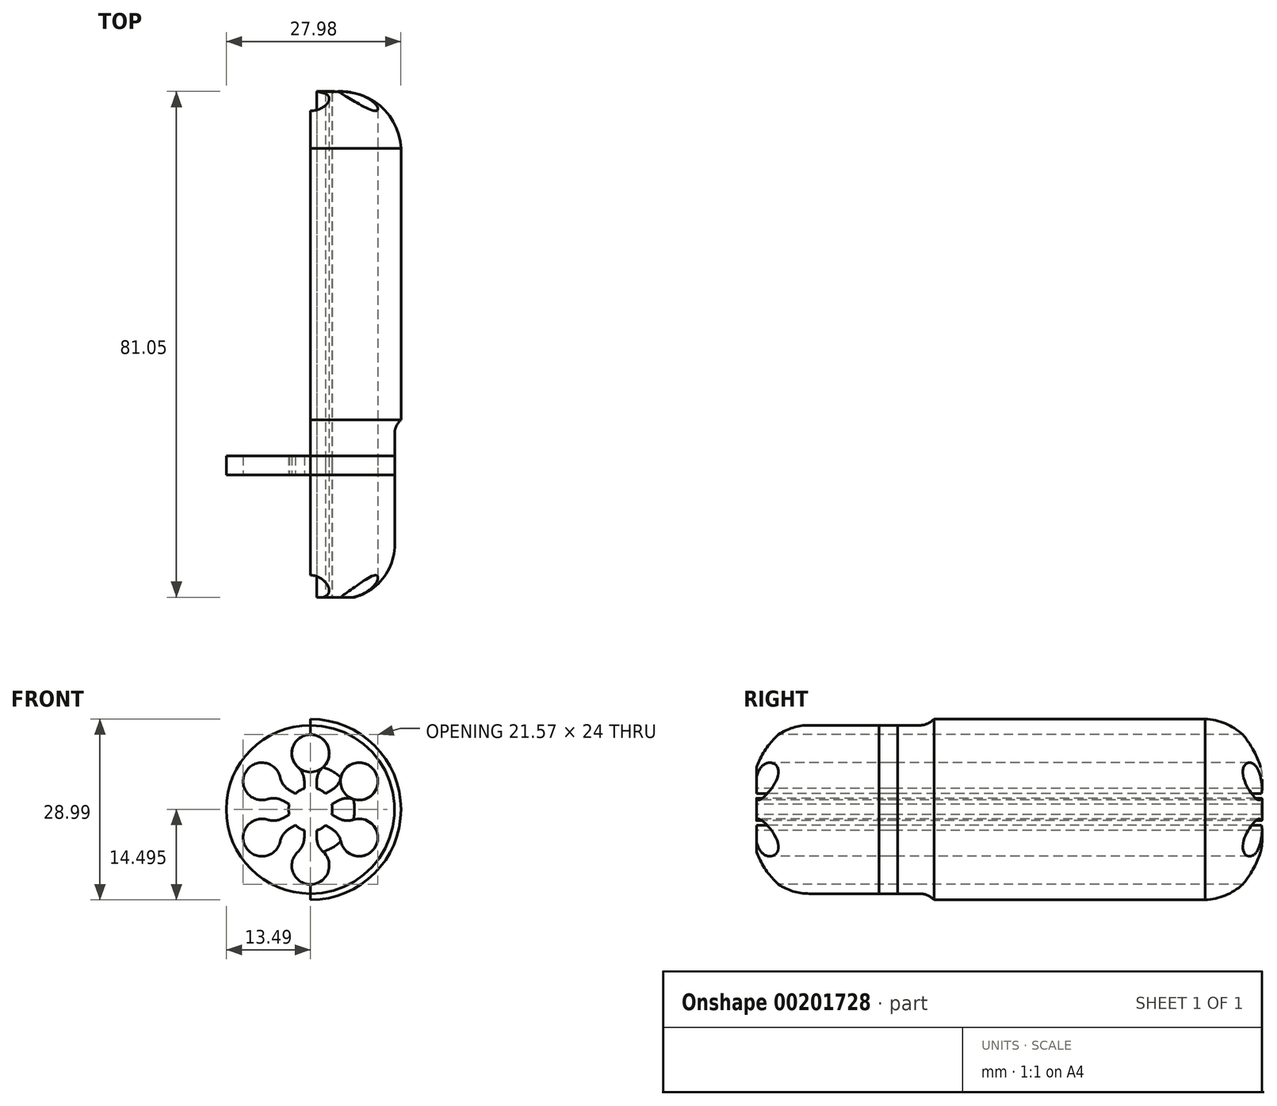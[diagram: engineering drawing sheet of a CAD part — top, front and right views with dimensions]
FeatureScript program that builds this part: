
annotation { "Feature Type Name" : "Feature", "Feature Type Description" : "" }
export const myFeature = defineFeature(function(context is Context, id is Id, definition is map)
    precondition{}
    {
        {
            var Q0;
            Q0=qCreatedBy(makeId("Right.planeOp"),FACE);
            var sketch = newSketch(context, id + "F0", { "sketchPlane" : qUnion([Q0])});
            skLineSegment(sketch, "E0.bottom", {"start": v(-3.13, 33.38) * mm, "end": v(86.87, 33.38) * mm});
            skLineSegment(sketch, "E0.top", {"start": v(-3.13, 32.38) * mm, "end": v(4.08, 32.38) * mm});
            skLineSegment(sketch, "E0.left", {"start": v(-3.13, 33.38) * mm, "end": v(-3.13, 32.38) * mm});
            skLineSegment(sketch, "E0.right", {"start": v(86.87, 33.38) * mm, "end": v(86.87, 32.38) * mm});
            skPoint(sketch, "E0.middle", {"position": v(41.87, 32.88) * mm});
            skLineSegment(sketch, "E1.bottom", {"start": v(86.87, 32.38) * mm, "end": v(81.87, 32.38) * mm, "construction": true});
            skLineSegment(sketch, "E1.top", {"start": v(86.87, 21.38) * mm, "end": v(85.87, 21.38) * mm});
            skLineSegment(sketch, "E1.left", {"start": v(86.87, 32.38) * mm, "end": v(86.87, 21.38) * mm, "construction": true});
            skLineSegment(sketch, "E1.right", {"start": v(81.87, 32.38) * mm, "end": v(81.87, 21.38) * mm, "construction": true});
            skLineSegment(sketch, "E2.bottom", {"start": v(81.87, 32.38) * mm, "end": v(71.87, 32.38) * mm, "construction": true});
            skLineSegment(sketch, "E2.top", {"start": v(81.87, 21.38) * mm, "end": v(71.87, 21.38) * mm, "construction": true});
            skLineSegment(sketch, "E2.right", {"start": v(71.87, 33.38) * mm, "end": v(71.87, 21.38) * mm, "construction": true});
            skLineSegment(sketch, "E3.0", {"start": v(85.87, 22.38) * mm, "end": v(85.37, 22.38) * mm, "construction": true});
            skLineSegment(sketch, "E4.0", {"start": v(85.87, 32.38) * mm, "end": v(85.87, 21.38) * mm, "construction": true});
            skArc(sketch, "E5", {"start": v(82.3, 22.38) * mm, "mid": v(80.84, 28.3) * mm, "end": v(76.33, 32.38) * mm});
            skArc(sketch, "E6", {"start": v(81.87, 21.38) * mm, "mid": v(79.3, 29.1) * mm, "end": v(71.87, 32.38) * mm});
            skLineSegment(sketch, "E7.trimOffspring", {"start": v(76.33, 32.38) * mm, "end": v(86.87, 32.38) * mm});
            skLineSegment(sketch, "E8.top", {"start": v(86.87, 25.38) * mm, "end": v(85.87, 25.38) * mm});
            skLineSegment(sketch, "E8.left", {"start": v(86.87, 23.38) * mm, "end": v(86.87, 25.38) * mm});
            skLineSegment(sketch, "E8.right", {"start": v(85.87, 22.38) * mm, "end": v(85.87, 22.72) * mm, "construction": true});
            skLineSegment(sketch, "E9.bottom", {"start": v(-3.13, 32.38) * mm, "end": v(-2.13, 32.38) * mm, "construction": true});
            skLineSegment(sketch, "E9.top", {"start": v(-3.13, 21.38) * mm, "end": v(-2.13, 21.38) * mm});
            skLineSegment(sketch, "E9.left", {"start": v(-3.13, 32.38) * mm, "end": v(-3.13, 21.38) * mm, "construction": true});
            skLineSegment(sketch, "E9.right", {"start": v(-2.13, 32.38) * mm, "end": v(-2.13, 21.38) * mm, "construction": true});
            skLineSegment(sketch, "E10.bottom", {"start": v(-2.13, 32.38) * mm, "end": v(4.08, 32.38) * mm, "construction": true});
            skLineSegment(sketch, "E10.top", {"start": v(-2.13, 33.38) * mm, "end": v(8.87, 33.38) * mm, "construction": true});
            skLineSegment(sketch, "E10.left", {"start": v(-2.13, 32.38) * mm, "end": v(-2.13, 33.38) * mm, "construction": true});
            skLineSegment(sketch, "E10.right", {"start": v(8.87, 32.38) * mm, "end": v(8.87, 33.38) * mm, "construction": true});
            skArc(sketch, "E11", {"start": v(4.08, 32.38) * mm, "mid": v(-1.17, 27.96) * mm, "end": v(-3.13, 21.38) * mm});
            skArc(sketch, "E12", {"start": v(8.87, 32.38) * mm, "mid": v(1.1, 29.16) * mm, "end": v(-2.13, 21.38) * mm});
            skLineSegment(sketch, "E13.trimOffspring", {"start": v(8.87, 32.38) * mm, "end": v(71.87, 32.38) * mm});
            skLineSegment(sketch, "E14", {"start": v(8.87, 21.38) * mm, "end": v(71.87, 21.38) * mm, "construction": true});
            skLineSegment(sketch, "E15.0", {"start": v(8.87, 17.38) * mm, "end": v(71.87, 17.38) * mm, "construction": true});
            skLineSegment(sketch, "E16.0", {"start": v(86.87, 23.38) * mm, "end": v(85.87, 23.38) * mm, "construction": true});
            skLineSegment(sketch, "E17.0", {"start": v(83.87, 21.38) * mm, "end": v(83.87, 25.38) * mm, "construction": true});
            skLineSegment(sketch, "E18", {"start": v(86.87, 23.38) * mm, "end": v(83.87, 21.38) * mm});
            skLineSegment(sketch, "E19.0", {"start": v(85.87, 23.92) * mm, "end": v(83.57, 22.38) * mm});
            skLineSegment(sketch, "E20.trimOffspring", {"start": v(83.87, 21.38) * mm, "end": v(81.87, 21.38) * mm});
            skLineSegment(sketch, "E21.trimOffspring", {"start": v(83.57, 22.38) * mm, "end": v(82.3, 22.38) * mm});
            skLineSegment(sketch, "E22.trimOffspring", {"start": v(85.87, 23.92) * mm, "end": v(85.87, 25.38) * mm});
            skLineSegment(sketch, "E23.bottom", {"start": v(8.87, 17.38) * mm, "end": v(-3.13, 17.38) * mm, "construction": true});
            skLineSegment(sketch, "E23.top", {"start": v(8.87, 21.38) * mm, "end": v(-3.13, 21.38) * mm, "construction": true});
            skLineSegment(sketch, "E23.left", {"start": v(8.87, 17.38) * mm, "end": v(8.87, 21.38) * mm, "construction": true});
            skLineSegment(sketch, "E23.right", {"start": v(-3.13, 17.38) * mm, "end": v(-3.13, 21.38) * mm, "construction": true});
            skSolve(sketch);
        }
        {
            var Q0;
            Q0=qCreatedBy(makeId("Right.planeOp"),FACE);
            var sketch = newSketch(context, id + "F1", { "sketchPlane" : qUnion([Q0])});
            skLineSegment(sketch, "E24.bottom", {"start": v(-3.13, 33.38) * mm, "end": v(28.58, 33.38) * mm, "construction": true});
            skLineSegment(sketch, "E24.left", {"start": v(-3.13, 33.38) * mm, "end": v(-3.13, 23.38) * mm, "construction": true});
            skLineSegment(sketch, "E24.right", {"start": v(28.58, 33.38) * mm, "end": v(28.58, 33.38) * mm});
            skLineSegment(sketch, "E25", {"start": v(28.58, 32.38) * mm, "end": v(8.84, 32.38) * mm, "construction": true});
            skArc(sketch, "E26", {"start": v(8.84, 32.38) * mm, "mid": v(1.84, 29.83) * mm, "end": v(-1.88, 23.38) * mm, "construction": true});
            skLineSegment(sketch, "E27.0", {"start": v(27.9, 31.88) * mm, "end": v(8.84, 31.88) * mm});
            skArc(sketch, "E28.0", {"start": v(8.84, 31.88) * mm, "mid": v(2.16, 29.45) * mm, "end": v(-1.38, 23.3) * mm});
            skLineSegment(sketch, "E29.0", {"start": v(26.58, 31.38) * mm, "end": v(8.84, 31.38) * mm});
            skArc(sketch, "E30.0", {"start": v(8.84, 30.88) * mm, "mid": v(2.9, 28.77) * mm, "end": v(-0.35, 23.38) * mm, "construction": true});
            skPoint(sketch, "E31.newPointB", {"position": v(28.58, 23.38) * mm});
            skArc(sketch, "E31.filletArc", {"start": v(26.58, 31.38) * mm, "mid": v(27.3, 31.5) * mm, "end": v(27.9, 31.88) * mm});
            skArc(sketch, "E32", {"start": v(8.84, 31.38) * mm, "mid": v(2.64, 29.01) * mm, "end": v(-0.4, 23.12) * mm});
            skLineSegment(sketch, "E33.trimOffspring", {"start": v(-1.37, 23.38) * mm, "end": v(-0.35, 23.38) * mm});
            skSolve(sketch);
        }
        {
            var Q0;
            Q0=qCreatedBy(makeId("Right.planeOp"),FACE);
            var sketch = newSketch(context, id + "F2", { "sketchPlane" : qUnion([Q0])});
            skLineSegment(sketch, "E34", {"start": v(86.87, 23.38) * mm, "end": v(83.87, 21.38) * mm, "construction": true});
            skLineSegment(sketch, "E35", {"start": v(83.87, 21.38) * mm, "end": v(81.87, 21.38) * mm, "construction": true});
            skLineSegment(sketch, "E36.0", {"start": v(86.87, 22.78) * mm, "end": v(84.02, 20.88) * mm});
            skLineSegment(sketch, "E37.0", {"start": v(84.02, 20.88) * mm, "end": v(81.87, 20.88) * mm});
            skLineSegment(sketch, "E38", {"start": v(86.87, 22.78) * mm, "end": v(86.87, 17.38) * mm});
            skLineSegment(sketch, "E39.0", {"start": v(66.87, 20.38) * mm, "end": v(66.87, 17.38) * mm});
            skLineSegment(sketch, "E40.0", {"start": v(81.87, 20.38) * mm, "end": v(66.87, 20.38) * mm});
            skLineSegment(sketch, "E41", {"start": v(71.87, 17.38) * mm, "end": v(66.87, 17.38) * mm});
            skLineSegment(sketch, "E42", {"start": v(71.87, 17.38) * mm, "end": v(86.87, 17.38) * mm});
            skLineSegment(sketch, "E43.0", {"start": v(81.87, 20.88) * mm, "end": v(81.87, 20.38) * mm});
            skSolve(sketch);
        }
        {
            var Q0;
            Q0=qCreatedBy(makeId("Right.planeOp"),FACE);
            var sketch = newSketch(context, id + "F3", { "sketchPlane" : qUnion([Q0])});
            skArc(sketch, "E44", {"start": v(81.87, 21.38) * mm, "mid": v(79.3, 29.1) * mm, "end": v(71.87, 32.38) * mm, "construction": true});
            skArc(sketch, "E45.0", {"start": v(81.3, 20.88) * mm, "mid": v(79.25, 28.4) * mm, "end": v(72.28, 31.88) * mm});
            skLineSegment(sketch, "E46", {"start": v(81.87, 20.38) * mm, "end": v(69.18, 20.38) * mm, "construction": true});
            skLineSegment(sketch, "E47", {"start": v(28.58, 32.38) * mm, "end": v(37.05, 32.38) * mm});
            skLineSegment(sketch, "E48", {"start": v(26.58, 31.38) * mm, "end": v(22.5, 31.38) * mm});
            skArc(sketch, "E49", {"start": v(26.58, 31.38) * mm, "mid": v(27.7, 31.64) * mm, "end": v(28.58, 32.38) * mm});
            skLineSegment(sketch, "E50.0", {"start": v(28.58, 31.88) * mm, "end": v(72.28, 31.88) * mm});
            skArc(sketch, "E51.0", {"start": v(26.58, 30.88) * mm, "mid": v(27.93, 31.2) * mm, "end": v(28.98, 32.08) * mm});
            skLineSegment(sketch, "E52.0", {"start": v(26.58, 30.88) * mm, "end": v(8.74, 30.88) * mm});
            skLineSegment(sketch, "E53.0", {"start": v(81.3, 20.88) * mm, "end": v(0.37, 20.88) * mm});
            skArc(sketch, "E54", {"start": v(8.84, 31.38) * mm, "mid": v(2.74, 29.11) * mm, "end": v(-0.35, 23.38) * mm, "construction": true});
            skArc(sketch, "E55.0", {"start": v(8.83, 30.88) * mm, "mid": v(3.5, 29.1) * mm, "end": v(0.37, 24.44) * mm});
            skLineSegment(sketch, "E56", {"start": v(-2.13, 27.58) * mm, "end": v(-2.13, 15.19) * mm, "construction": true});
            skLineSegment(sketch, "E57.trimOffspring", {"start": v(0.37, 24.44) * mm, "end": v(0.37, 20.88) * mm});
            skSolve(sketch);
        }
        {
            var Q0;
            Q0=qSketchRegion(id+"F3",true);
            var Q1;
            Q1=sQuery(id+"F0.wireOp",EDGE,"E15.0");
            revolve(context, id + "F4", {"entities" : qUnion([Q0]), "axis" : qUnion([Q1]), "revolveType" : RevolveType.ONE_DIRECTION, "angle" : 180 * degree});
        }
        {
            var Q0;
            Q0=qCreatedBy(makeId("Front.planeOp"),FACE);
            var sketch = newSketch(context, id + "F5", { "sketchPlane" : qUnion([Q0])});
            skCircle(sketch, "E58", {"center": v(0, 17.38) * mm, "radius": 14.5 * mm, "construction": true});
            skCircle(sketch, "E59", {"center": v(0, 17.38) * mm, "radius": 3.5 * mm});
            skLineSegment(sketch, "E60", {"start": v(0, 17.38) * mm, "end": v(0, 5.38) * mm, "construction": true});
            skPoint(sketch, "E61", {"position": v(0, 5.38) * mm});
            skPoint(sketch, "E62", {"position": v(-16.26, 26.77) * mm});
            skLineSegment(sketch, "E63.0", {"start": v(-1, 14.03) * mm, "end": v(-1, 12.86) * mm});
            skLineSegment(sketch, "E64.0", {"start": v(1, 14.03) * mm, "end": v(1, 12.86) * mm});
            skArc(sketch, "E65", {"start": v(-2, 10.62) * mm, "mid": v(0, 5.38) * mm, "end": v(2, 10.62) * mm});
            skPoint(sketch, "E66.visualSharp", {"position": v(-1, 11.21) * mm});
            skArc(sketch, "E66.filletArc", {"start": v(-2, 10.62) * mm, "mid": v(-1.26, 11.63) * mm, "end": v(-1, 12.86) * mm});
            skPoint(sketch, "E67.visualSharp", {"position": v(1, 11.21) * mm});
            skArc(sketch, "E67.filletArc", {"start": v(1, 12.86) * mm, "mid": v(1.26, 11.63) * mm, "end": v(2, 10.62) * mm});
            skSolve(sketch);
        }
        {
            var Q0;
            {var subQ0=sQuery(id+"F5.wireOp",EDGE,"E63.0");Q0=makeQuery(id+"F5.imprint","IMPRINT",FACE,{"disambiguationData":[TD([[makeQuery(id+"F5.imprint","IMPRINT",EDGE,{"derivedFrom":subQ0}),1.0]])]});}
            extrude(context, id + "F6", {"entities" : qUnion([Q0]), "oppositeDirection" : true, "depth" : 90 * mm});
        }
        {
            var Q0;
            Q0=qCreatedBy(makeId("Right.planeOp"),FACE);
            var sketch = newSketch(context, id + "F7", { "sketchPlane" : qUnion([Q0])});
            skLineSegment(sketch, "E68", {"start": v(0, 17.38) * mm, "end": v(41.07, 17.38) * mm});
            skSolve(sketch);
        }
        {
            var Q0;
            Q0=makeQuery(id+"F6.opExtrude","SWEPT_BODY",BODY,{"disambiguationData":[OSD([sQuery(id+"F5.wireOp",EDGE,"E59"),sQuery(id+"F5.wireOp",EDGE,"E63.0"),sQuery(id+"F5.wireOp",EDGE,"E64.0"),sQuery(id+"F5.wireOp",EDGE,"E65")])]});
            var Q1;
            Q1=sQuery(id+"F7.wireOp",EDGE,"E68");
            circularPattern(context, id + "F8", {"entities" : qUnion([Q0]), "axis" : qUnion([Q1]), "angle" : 360 * degree, "instanceCount" : 6, "equalSpace" : true});
        }
        {
            var Q0;
            Q0=makeQuery(id+"F8.opPattern","COPY",BODY,{"derivedFrom":makeQuery(id+"F6.opExtrude","SWEPT_BODY",BODY,{"disambiguationData":[OSD([sQuery(id+"F5.wireOp",EDGE,"E59"),sQuery(id+"F5.wireOp",EDGE,"E63.0"),sQuery(id+"F5.wireOp",EDGE,"E64.0"),sQuery(id+"F5.wireOp",EDGE,"E65"),sQuery(id+"F5.wireOp",EDGE,"E66.filletArc"),sQuery(id+"F5.wireOp",EDGE,"E67.filletArc")])]}),"instanceName":"3"});
            var Q1;
            Q1=makeQuery(id+"F8.opPattern","COPY",BODY,{"derivedFrom":makeQuery(id+"F6.opExtrude","SWEPT_BODY",BODY,{"disambiguationData":[OSD([sQuery(id+"F5.wireOp",EDGE,"E59"),sQuery(id+"F5.wireOp",EDGE,"E63.0"),sQuery(id+"F5.wireOp",EDGE,"E64.0"),sQuery(id+"F5.wireOp",EDGE,"E65"),sQuery(id+"F5.wireOp",EDGE,"E66.filletArc"),sQuery(id+"F5.wireOp",EDGE,"E67.filletArc")])]}),"instanceName":"4"});
            var Q2;
            Q2=makeQuery(id+"F8.opPattern","COPY",BODY,{"derivedFrom":makeQuery(id+"F6.opExtrude","SWEPT_BODY",BODY,{"disambiguationData":[OSD([sQuery(id+"F5.wireOp",EDGE,"E59"),sQuery(id+"F5.wireOp",EDGE,"E63.0"),sQuery(id+"F5.wireOp",EDGE,"E64.0"),sQuery(id+"F5.wireOp",EDGE,"E65"),sQuery(id+"F5.wireOp",EDGE,"E66.filletArc"),sQuery(id+"F5.wireOp",EDGE,"E67.filletArc")])]}),"instanceName":"5"});
            var Q3;
            Q3=makeQuery(id+"F6.opExtrude","SWEPT_BODY",BODY,{"disambiguationData":[OSD([sQuery(id+"F5.wireOp",EDGE,"E59"),sQuery(id+"F5.wireOp",EDGE,"E63.0"),sQuery(id+"F5.wireOp",EDGE,"E64.0"),sQuery(id+"F5.wireOp",EDGE,"E65"),sQuery(id+"F5.wireOp",EDGE,"E66.filletArc"),sQuery(id+"F5.wireOp",EDGE,"E67.filletArc")])]});
            var Q4;
            Q4=makeQuery(id+"F4.opRevolve","SWEPT_BODY",BODY,{"disambiguationData":[OSD([sQuery(id+"F3.wireOp",EDGE,"E45.0"),sQuery(id+"F3.wireOp",EDGE,"E50.0"),sQuery(id+"F3.wireOp",EDGE,"E51.0"),sQuery(id+"F3.wireOp",EDGE,"E52.0"),sQuery(id+"F3.wireOp",EDGE,"E53.0"),sQuery(id+"F3.wireOp",EDGE,"E55.0"),sQuery(id+"F3.wireOp",EDGE,"E57.trimOffspring")])]});
            booleanBodies(context, id + "F9", {"operationType" : BooleanOperationType.SUBTRACTION, "tools" : qUnion([Q0, Q1, Q2, Q3]), "targets" : qUnion([Q4]), "keepTools" : true});
        }
        {
            var Q0;
            Q0 = qSketchRegion(id + "F3", true);
            var Q1;
            Q1=sQuery(id+"F0.wireOp",EDGE,"E15.0");
            revolve(context, id + "F10", {"entities" : qUnion([Q0]), "axis" : qUnion([Q1]), "revolveType" : RevolveType.FULL});
        }
        {
            var Q0;
            Q0=qCreatedBy(makeId("Front.planeOp"),FACE);
            var sketch = newSketch(context, id + "F11", { "sketchPlane" : qUnion([Q0])});
            skCircle(sketch, "E69.0", {"center": v(0, 17.38) * mm, "radius": 13.5 * mm});
            skSolve(sketch);
        }
        {
            var Q0;
            Q0 = qSketchRegion(id + "F11", true);
            extrude(context, id + "F12", {"entities" : qUnion([Q0]), "oppositeDirection" : true, "depth" : 23 * mm, "hasSecondDirection" : true, "secondDirectionOppositeDirection" : true, "secondDirectionDepth" : 20 * mm});
        }
        {
            var Q0;
            Q0=makeQuery(id+"F6.opExtrude","SWEPT_BODY",BODY,{"disambiguationData":[OSD([sQuery(id+"F5.wireOp",EDGE,"E59"),sQuery(id+"F5.wireOp",EDGE,"E63.0"),sQuery(id+"F5.wireOp",EDGE,"E64.0"),sQuery(id+"F5.wireOp",EDGE,"E65"),sQuery(id+"F5.wireOp",EDGE,"E66.filletArc"),sQuery(id+"F5.wireOp",EDGE,"E67.filletArc")])]});
            var Q1;
            Q1=makeQuery(id+"F8.opPattern","COPY",BODY,{"derivedFrom":makeQuery(id+"F6.opExtrude","SWEPT_BODY",BODY,{"disambiguationData":[OSD([sQuery(id+"F5.wireOp",EDGE,"E59"),sQuery(id+"F5.wireOp",EDGE,"E63.0"),sQuery(id+"F5.wireOp",EDGE,"E64.0"),sQuery(id+"F5.wireOp",EDGE,"E65"),sQuery(id+"F5.wireOp",EDGE,"E66.filletArc"),sQuery(id+"F5.wireOp",EDGE,"E67.filletArc")])]}),"instanceName":"5"});
            var Q2;
            Q2=makeQuery(id+"F8.opPattern","COPY",BODY,{"derivedFrom":makeQuery(id+"F6.opExtrude","SWEPT_BODY",BODY,{"disambiguationData":[OSD([sQuery(id+"F5.wireOp",EDGE,"E59"),sQuery(id+"F5.wireOp",EDGE,"E63.0"),sQuery(id+"F5.wireOp",EDGE,"E64.0"),sQuery(id+"F5.wireOp",EDGE,"E65"),sQuery(id+"F5.wireOp",EDGE,"E66.filletArc"),sQuery(id+"F5.wireOp",EDGE,"E67.filletArc")])]}),"instanceName":"4"});
            var Q3;
            Q3=makeQuery(id+"F8.opPattern","COPY",BODY,{"derivedFrom":makeQuery(id+"F6.opExtrude","SWEPT_BODY",BODY,{"disambiguationData":[OSD([sQuery(id+"F5.wireOp",EDGE,"E59"),sQuery(id+"F5.wireOp",EDGE,"E63.0"),sQuery(id+"F5.wireOp",EDGE,"E64.0"),sQuery(id+"F5.wireOp",EDGE,"E65"),sQuery(id+"F5.wireOp",EDGE,"E66.filletArc"),sQuery(id+"F5.wireOp",EDGE,"E67.filletArc")])]}),"instanceName":"3"});
            var Q4;
            Q4=makeQuery(id+"F8.opPattern","COPY",BODY,{"derivedFrom":makeQuery(id+"F6.opExtrude","SWEPT_BODY",BODY,{"disambiguationData":[OSD([sQuery(id+"F5.wireOp",EDGE,"E59"),sQuery(id+"F5.wireOp",EDGE,"E63.0"),sQuery(id+"F5.wireOp",EDGE,"E64.0"),sQuery(id+"F5.wireOp",EDGE,"E65"),sQuery(id+"F5.wireOp",EDGE,"E66.filletArc"),sQuery(id+"F5.wireOp",EDGE,"E67.filletArc")])]}),"instanceName":"2"});
            var Q5;
            Q5=makeQuery(id+"F8.opPattern","COPY",BODY,{"derivedFrom":makeQuery(id+"F6.opExtrude","SWEPT_BODY",BODY,{"disambiguationData":[OSD([sQuery(id+"F5.wireOp",EDGE,"E59"),sQuery(id+"F5.wireOp",EDGE,"E63.0"),sQuery(id+"F5.wireOp",EDGE,"E64.0"),sQuery(id+"F5.wireOp",EDGE,"E65"),sQuery(id+"F5.wireOp",EDGE,"E66.filletArc"),sQuery(id+"F5.wireOp",EDGE,"E67.filletArc")])]}),"instanceName":"1"});
            var Q6;
            Q6=makeQuery(id+"F10.opRevolve","SWEPT_BODY",BODY,{"disambiguationData":[OSD([sQuery(id+"F3.wireOp",EDGE,"E45.0"),sQuery(id+"F3.wireOp",EDGE,"E50.0"),sQuery(id+"F3.wireOp",EDGE,"E51.0"),sQuery(id+"F3.wireOp",EDGE,"E52.0"),sQuery(id+"F3.wireOp",EDGE,"E53.0"),sQuery(id+"F3.wireOp",EDGE,"E55.0"),sQuery(id+"F3.wireOp",EDGE,"E57.trimOffspring")])]});
            booleanBodies(context, id + "F13", {"operationType" : BooleanOperationType.SUBTRACTION, "tools" : qUnion([Q0, Q1, Q2, Q3, Q4, Q5]), "targets" : qUnion([Q6])});
        }
        {
            var Q0;
            Q0=makeQuery(id+"F10.opRevolve","SWEPT_BODY",BODY,{"disambiguationData":[OSD([sQuery(id+"F3.wireOp",EDGE,"E45.0"),sQuery(id+"F3.wireOp",EDGE,"E50.0"),sQuery(id+"F3.wireOp",EDGE,"E51.0"),sQuery(id+"F3.wireOp",EDGE,"E52.0"),sQuery(id+"F3.wireOp",EDGE,"E53.0"),sQuery(id+"F3.wireOp",EDGE,"E55.0"),sQuery(id+"F3.wireOp",EDGE,"E57.trimOffspring")])]});
            var Q1;
            Q1=makeQuery(id+"F12.opExtrude","SWEPT_BODY",BODY,{"disambiguationData":[OSD([sQuery(id+"F11.wireOp",EDGE,"E69.0")])]});
            booleanBodies(context, id + "F14", {"operationType" : BooleanOperationType.INTERSECTION, "tools" : qUnion([Q0, Q1])});
        }
    });
